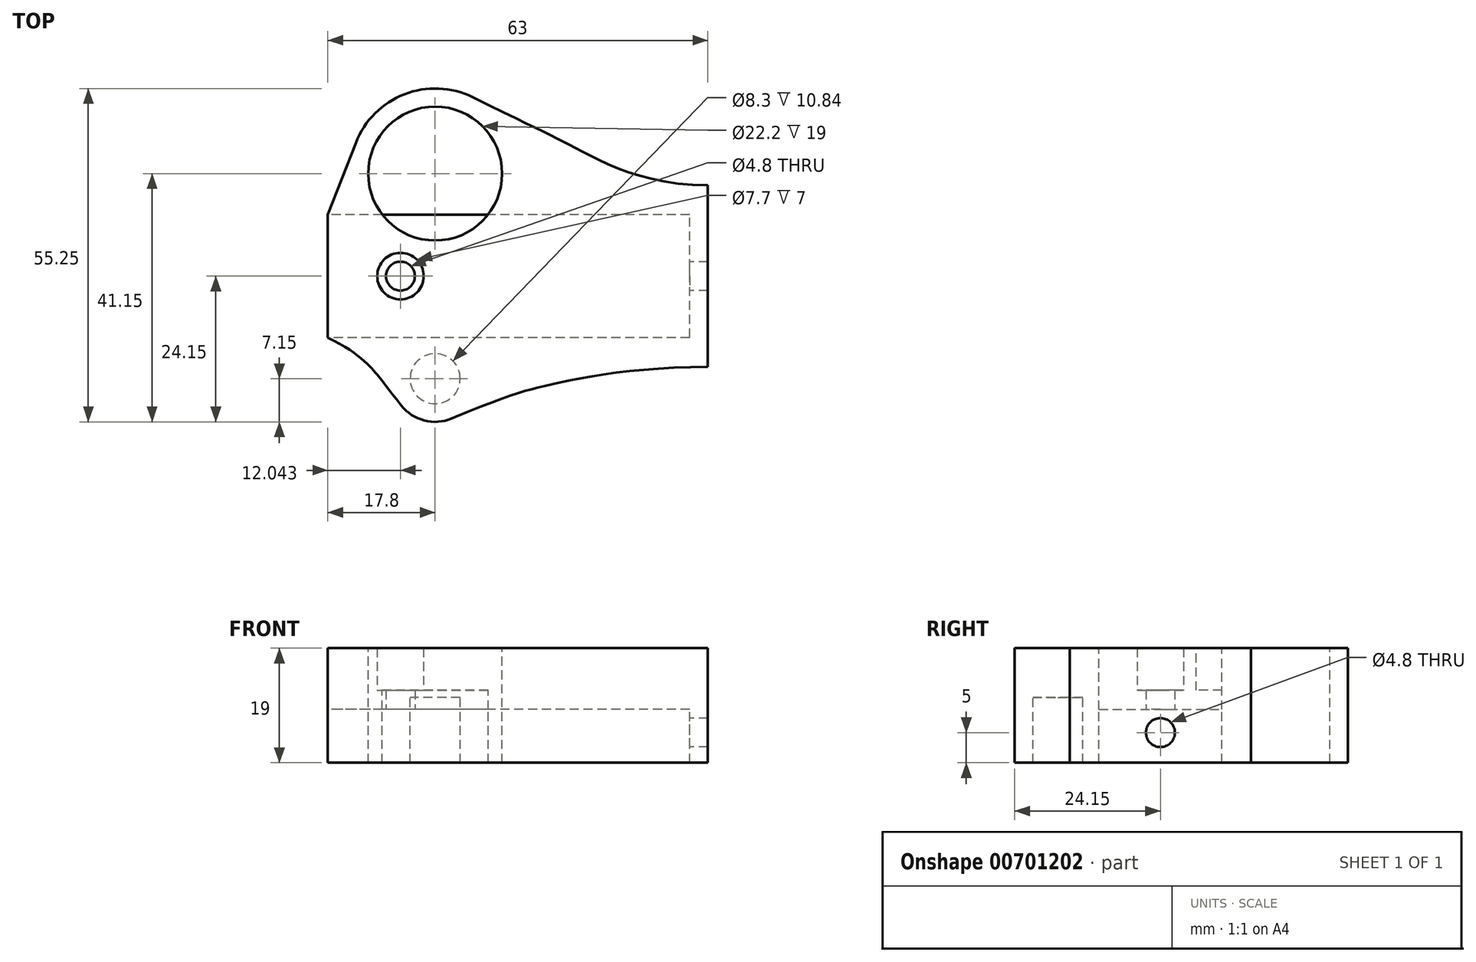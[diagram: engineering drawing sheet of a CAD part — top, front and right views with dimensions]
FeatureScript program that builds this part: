
annotation { "Feature Type Name" : "Feature", "Feature Type Description" : "" }
export const myFeature = defineFeature(function(context is Context, id is Id, definition is map)
    precondition{}
    {
        {
            var Q0;
            Q0=qCreatedBy(makeId("Top.planeOp"),FACE);
            var sketch = newSketch(context, id + "F0", { "sketchPlane" : qUnion([Q0])});
            skCircle(sketch, "E0", {"center": v(-12.2, 17) * mm, "radius": 4 * mm});
            skCircle(sketch, "E1", {"center": v(-12.2, -17) * mm, "radius": 4.15 * mm});
            skLineSegment(sketch, "E2.bottom", {"start": v(30, -10.2) * mm, "end": v(-30, -10.2) * mm});
            skLineSegment(sketch, "E2.top", {"start": v(30, 10.2) * mm, "end": v(-30, 10.2) * mm});
            skLineSegment(sketch, "E2.left", {"start": v(30, -10.2) * mm, "end": v(30, 10.2) * mm});
            skLineSegment(sketch, "E2.right", {"start": v(-30, -10.2) * mm, "end": v(-30, 10.2) * mm});
            skPoint(sketch, "E2.middle", {"position": v(0, 0) * mm});
            skCircle(sketch, "E3", {"center": v(-12.2, 17) * mm, "radius": 11.1 * mm});
            skLineSegment(sketch, "E4", {"start": v(33, 15.04) * mm, "end": v(33, -15.04) * mm});
            skArc(sketch, "E5", {"start": v(-19.16, -18.64) * mm, "mid": v(-14.38, -23.81) * mm, "end": v(-7.49, -22.38) * mm});
            skFitSpline(sketch, "E6", {"points": [v(-9.48, -23.61) * mm, v(6.11, -18.17) * mm, v(33, -15.04) * mm], "startDerivative": vector(64.87, 26.65) * mm, "endDerivative": vector(67.24, 0) * mm});
            skFitSpline(sketch, "E7", {"points": [v(-17.8, -21.45) * mm, v(-22.33, -15.73) * mm, v(-30, -10.2) * mm], "startDerivative": vector(-19.8, 24.95) * mm, "endDerivative": vector(-24.6, 11.58) * mm});
            skFitSpline(sketch, "E8", {"points": [v(-6.72, 30.02) * mm, v(11.05, 21.24) * mm, v(33, 15.04) * mm], "startDerivative": vector(71.44, -35.14) * mm, "endDerivative": vector(61.13, 0) * mm});
            skCircle(sketch, "E9", {"center": v(-12.2, 17) * mm, "radius": 14.1 * mm});
            skLineSegment(sketch, "E10", {"start": v(-30, 10.2) * mm, "end": v(-25.33, 22.14) * mm});
            skSolve(sketch);
        }
        {
            var Q0;
            Q0=makeQuery(id+"F0.imprint","IMPRINT",FACE,{"disambiguationData":[TD([[makeQuery(id+"F0.imprint","IMPRINT",EDGE,{"derivedFrom":sQuery(id+"F0.wireOp",EDGE,"E1")}),-1.0]])]});
            var Q1;
            {var subQ0=sQuery(id+"F0.wireOp",EDGE,"E9");var subQ4=sQuery(id+"F0.wireOp",EDGE,"E2.top");var subQ8=makeQuery(id+"F0.imprint","INTERSECT",VERTEX,{"disambiguationData":[OD(0.0)],"derivedFrom":[subQ4,subQ0]});Q1=makeQuery(id+"F0.imprint","IMPRINT",FACE,{"disambiguationData":[TD([[makeQuery(id+"F0.imprint","IMPRINT",EDGE,{"disambiguationData":[TD([[subQ8,-1.0]])],"derivedFrom":subQ4}),-1.0]])]});}
            var Q2;
            {var subQ0=sQuery(id+"F0.wireOp",EDGE,"E10");Q2=makeQuery(id+"F0.imprint","IMPRINT",FACE,{"disambiguationData":[TD([[makeQuery(id+"F0.imprint","IMPRINT",EDGE,{"derivedFrom":subQ0}),-1.0]])]});}
            extrude(context, id + "F1", {"entities" : qUnion([Q0, Q1, Q2]), "oppositeDirection" : true, "depth" : 12 * mm, "offsetDistance" : 25 * mm});
        }
        {
            var Q0;
            Q0=makeQuery(id+"F0.imprint","IMPRINT",FACE,{"disambiguationData":[TD([[makeQuery(id+"F0.imprint","IMPRINT",EDGE,{"derivedFrom":sQuery(id+"F0.wireOp",EDGE,"E2.bottom")}),-1.0]])]});
            var Q1;
            {var subQ0=sQuery(id+"F0.wireOp",EDGE,"E9");var subQ1=sQuery(id+"F0.wireOp",EDGE,"E2.top");var subQ2=makeQuery(id+"F0.imprint","INTERSECT",VERTEX,{"disambiguationData":[OD(0.0)],"derivedFrom":[subQ1,subQ0]});Q1=makeQuery(id+"F0.imprint","IMPRINT",FACE,{"disambiguationData":[TD([[makeQuery(id+"F0.imprint","IMPRINT",EDGE,{"disambiguationData":[TD([[subQ2,-1.0]])],"derivedFrom":subQ1}),1.0]])]});}
            var Q2;
            {var subQ0=sQuery(id+"F0.wireOp",EDGE,"E3");var subQ1=sQuery(id+"F0.wireOp",EDGE,"E2.top");var subQ2=makeQuery(id+"F0.imprint","INTERSECT",VERTEX,{"disambiguationData":[OD(0.0)],"derivedFrom":[subQ1,subQ0]});Q2=makeQuery(id+"F0.imprint","IMPRINT",FACE,{"disambiguationData":[TD([[makeQuery(id+"F0.imprint","IMPRINT",EDGE,{"disambiguationData":[TD([[subQ2,-1.0]])],"derivedFrom":subQ1}),1.0]])]});}
            var Q3;
            Q3=makeQuery(id+"F0.imprint","IMPRINT",FACE,{"disambiguationData":[TD([[makeQuery(id+"F0.imprint","IMPRINT",EDGE,{"derivedFrom":sQuery(id+"F0.wireOp",EDGE,"E1")}),1.0]])]});
            extrude(context, id + "F2", {"entities" : qUnion([Q0, Q1, Q2, Q3]), "operationType" : NewBodyOperationType.ADD, "oppositeDirection" : true, "depth" : 3.16 * mm, "offsetDistance" : 25 * mm});
        }
        {
            var Q0;
            {var subQ0=sQuery(id+"F0.wireOp",EDGE,"E9");var subQ4=sQuery(id+"F0.wireOp",EDGE,"E2.top");var subQ8=makeQuery(id+"F0.imprint","INTERSECT",VERTEX,{"disambiguationData":[OD(0.0)],"derivedFrom":[subQ4,subQ0]});Q0=makeQuery(id+"F0.imprint","IMPRINT",FACE,{"disambiguationData":[TD([[makeQuery(id+"F0.imprint","IMPRINT",EDGE,{"disambiguationData":[TD([[subQ8,-1.0]])],"derivedFrom":subQ4}),-1.0]])]});}
            var Q1;
            {var subQ0=sQuery(id+"F0.wireOp",EDGE,"E9");var subQ1=sQuery(id+"F0.wireOp",EDGE,"E2.top");var subQ2=makeQuery(id+"F0.imprint","INTERSECT",VERTEX,{"disambiguationData":[OD(0.0)],"derivedFrom":[subQ1,subQ0]});Q1=makeQuery(id+"F0.imprint","IMPRINT",FACE,{"disambiguationData":[TD([[makeQuery(id+"F0.imprint","IMPRINT",EDGE,{"disambiguationData":[TD([[subQ2,-1.0]])],"derivedFrom":subQ1}),1.0]])]});}
            var Q2;
            Q2=makeQuery(id+"F0.imprint","IMPRINT",FACE,{"disambiguationData":[TD([[makeQuery(id+"F0.imprint","IMPRINT",EDGE,{"derivedFrom":sQuery(id+"F0.wireOp",EDGE,"E1")}),-1.0]])]});
            var Q3;
            Q3=makeQuery(id+"F0.imprint","IMPRINT",FACE,{"disambiguationData":[TD([[makeQuery(id+"F0.imprint","IMPRINT",EDGE,{"derivedFrom":sQuery(id+"F0.wireOp",EDGE,"E2.bottom")}),-1.0]])]});
            var Q4;
            {var subQ0=sQuery(id+"F0.wireOp",EDGE,"E10");Q4=makeQuery(id+"F0.imprint","IMPRINT",FACE,{"disambiguationData":[TD([[makeQuery(id+"F0.imprint","IMPRINT",EDGE,{"derivedFrom":subQ0}),-1.0]])]});}
            var Q5;
            Q5=makeQuery(id+"F0.imprint","IMPRINT",FACE,{"disambiguationData":[TD([[makeQuery(id+"F0.imprint","IMPRINT",EDGE,{"derivedFrom":sQuery(id+"F0.wireOp",EDGE,"E1")}),1.0]])]});
            extrude(context, id + "F3", {"entities" : qUnion([Q0, Q1, Q2, Q3, Q4, Q5]), "operationType" : NewBodyOperationType.ADD, "depth" : 7 * mm, "offsetDistance" : 25 * mm});
        }
        {
            var Q0;
            {var subQ0=sQuery(id+"F0.wireOp",EDGE,"E4");Q0=makeQuery(id+"F3.boolean.opBoolean","MERGE",FACE,{"derivedFrom":[makeQuery(id+"F1.opExtrude","SWEPT_FACE",FACE,{"disambiguationData":[OSD([subQ0])]}),makeQuery(id+"F3.opExtrude","SWEPT_FACE",FACE,{"disambiguationData":[OSD([subQ0])]})]});}
            var sketch = newSketch(context, id + "F4", { "sketchPlane" : qUnion([Q0])});
            skPoint(sketch, "E11", {"position": v(0, -7) * mm});
            skSolve(sketch);
        }
        {
            var Q0;
            Q0=makeQuery(id+"F3.opExtrude","CAP_FACE",FACE,{"disambiguationData":[OSD([sQuery(id+"F0.wireOp",EDGE,"E2.right"),sQuery(id+"F0.wireOp",EDGE,"E3"),sQuery(id+"F0.wireOp",EDGE,"E4"),sQuery(id+"F0.wireOp",EDGE,"E5"),sQuery(id+"F0.wireOp",EDGE,"E6"),sQuery(id+"F0.wireOp",EDGE,"E7"),sQuery(id+"F0.wireOp",EDGE,"E8"),sQuery(id+"F0.wireOp",EDGE,"E9"),sQuery(id+"F0.wireOp",EDGE,"E10")])],"isStart":false});
            var sketch = newSketch(context, id + "F5", { "sketchPlane" : qUnion([Q0])});
            skPoint(sketch, "E12", {"position": v(-17.96, 0) * mm});
            skSolve(sketch);
        }
        {
            var Q0;
            Q0=sQuery(id+"F5.wireOp",VERTEX,"E12");
            var Q1;
            Q1=makeQuery(id+"F1.opExtrude","SWEPT_BODY",BODY,{"disambiguationData":[OSD([sQuery(id+"F0.wireOp",EDGE,"E1"),sQuery(id+"F0.wireOp",EDGE,"E2.bottom"),sQuery(id+"F0.wireOp",EDGE,"E2.top"),sQuery(id+"F0.wireOp",EDGE,"E2.left"),sQuery(id+"F0.wireOp",EDGE,"E3"),sQuery(id+"F0.wireOp",EDGE,"E4"),sQuery(id+"F0.wireOp",EDGE,"E5"),sQuery(id+"F0.wireOp",EDGE,"E6"),sQuery(id+"F0.wireOp",EDGE,"E7"),sQuery(id+"F0.wireOp",EDGE,"E8"),sQuery(id+"F0.wireOp",EDGE,"E9"),sQuery(id+"F0.wireOp",EDGE,"E10")])]});
            hole(context, id + "F6", {"style" : HoleStyle.C_BORE, "endStyle" : HoleEndStyle.BLIND, "holeDiameter" : 4.8 * mm, "cBoreDiameter" : 7.7 * mm, "cBoreDepth" : 7 * mm, "majorDiameter" : 5 * mm, "holeDepth" : 15 * mm, "isTappedThrough" : true, "tappedDepth" : 12 * mm, "tapClearance" : 3, "locations" : qUnion([Q0]), "scope" : qUnion([Q1]), "startStyle" : HoleStartStyle.PART});
        }
        {
            var Q0;
            Q0=sQuery(id+"F4.wireOp",VERTEX,"E11");
            var Q1;
            Q1=makeQuery(id+"F1.opExtrude","SWEPT_BODY",BODY,{"disambiguationData":[OSD([sQuery(id+"F0.wireOp",EDGE,"E1"),sQuery(id+"F0.wireOp",EDGE,"E2.bottom"),sQuery(id+"F0.wireOp",EDGE,"E2.top"),sQuery(id+"F0.wireOp",EDGE,"E2.left"),sQuery(id+"F0.wireOp",EDGE,"E3"),sQuery(id+"F0.wireOp",EDGE,"E4"),sQuery(id+"F0.wireOp",EDGE,"E5"),sQuery(id+"F0.wireOp",EDGE,"E6"),sQuery(id+"F0.wireOp",EDGE,"E7"),sQuery(id+"F0.wireOp",EDGE,"E8"),sQuery(id+"F0.wireOp",EDGE,"E9"),sQuery(id+"F0.wireOp",EDGE,"E10")])]});
            hole(context, id + "F7", {"style" : HoleStyle.SIMPLE, "endStyle" : HoleEndStyle.BLIND, "holeDiameter" : 4.8 * mm, "majorDiameter" : 5 * mm, "holeDepth" : 10 * mm, "isTappedThrough" : true, "tappedDepth" : 12 * mm, "tapClearance" : 3, "locations" : qUnion([Q0]), "scope" : qUnion([Q1]), "startStyle" : HoleStartStyle.PART});
        }
        {
            var Q0;
            Q0=makeQuery(id+"F2.opExtrude","CAP_FACE",FACE,{"disambiguationData":[OSD([sQuery(id+"F0.wireOp",EDGE,"E1")])],"isStart":false});
            extrude(context, id + "F8", {"entities" : qUnion([Q0]), "operationType" : NewBodyOperationType.REMOVE, "oppositeDirection" : true, "depth" : 2 * mm, "offsetDistance" : 25 * mm});
        }
    });
